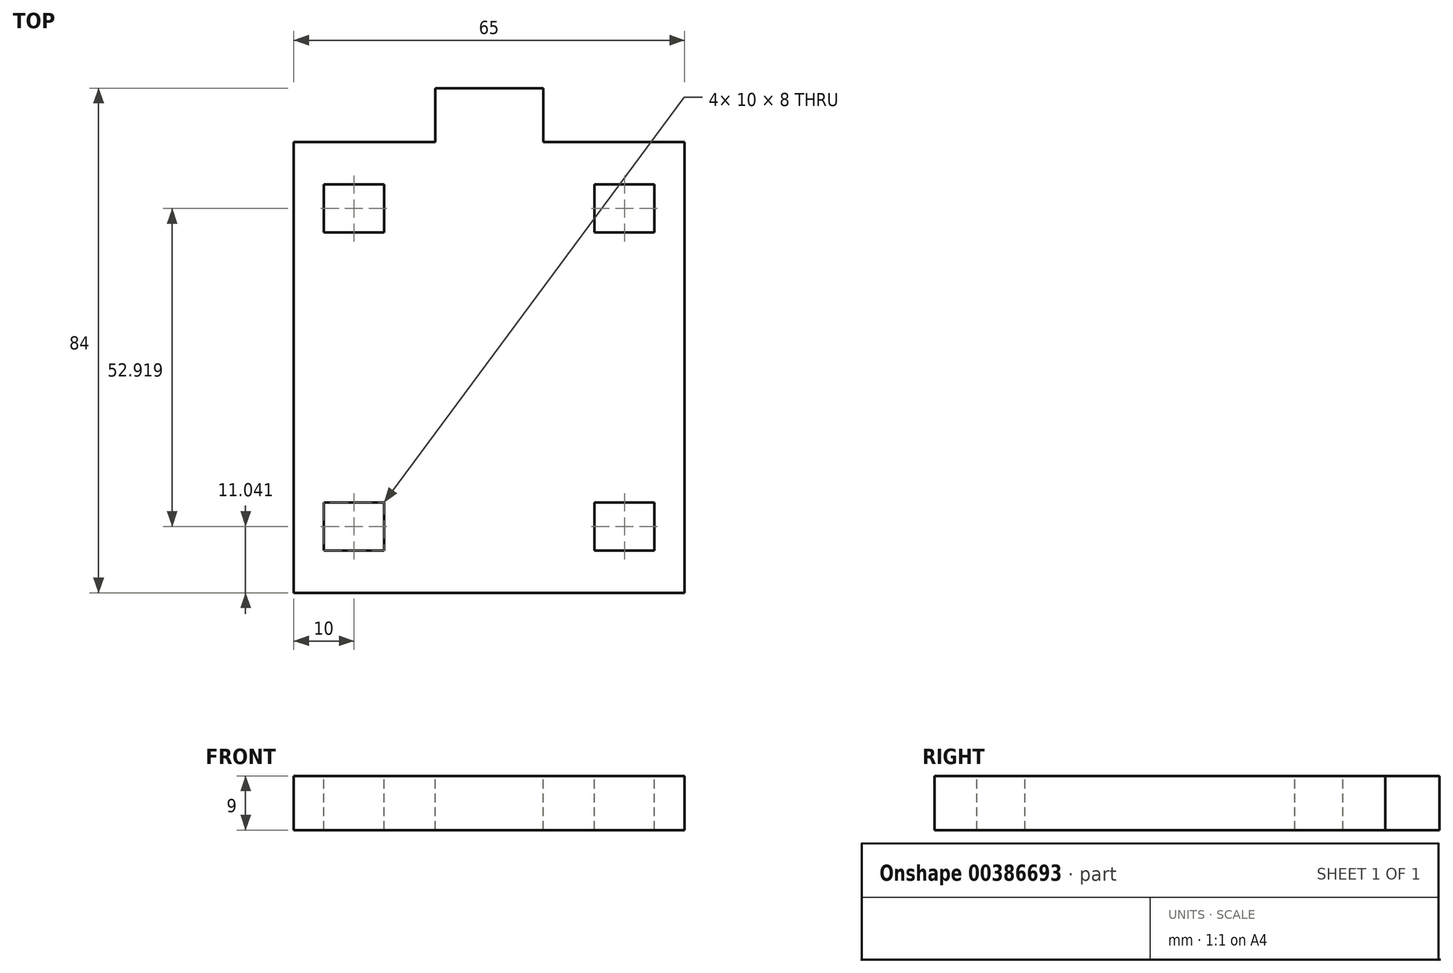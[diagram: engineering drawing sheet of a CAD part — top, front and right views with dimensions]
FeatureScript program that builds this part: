
annotation { "Feature Type Name" : "Feature", "Feature Type Description" : "" }
export const myFeature = defineFeature(function(context is Context, id is Id, definition is map)
    precondition{}
    {
        {
            var Q0;
            Q0=qCreatedBy(makeId("Top.planeOp"),FACE);
            var sketch = newSketch(context, id + "F0", { "sketchPlane" : qUnion([Q0])});
            skLineSegment(sketch, "E0.bottom", {"start": v(-32.5, 37.5) * mm, "end": v(32.5, 37.5) * mm});
            skLineSegment(sketch, "E0.top", {"start": v(-32.5, -37.5) * mm, "end": v(32.5, -37.5) * mm});
            skLineSegment(sketch, "E0.left", {"start": v(-32.5, 37.5) * mm, "end": v(-32.5, -37.5) * mm});
            skLineSegment(sketch, "E0.right", {"start": v(32.5, 37.5) * mm, "end": v(32.5, -37.5) * mm});
            skPoint(sketch, "E0.middle", {"position": v(0, 0) * mm});
            skSolve(sketch);
        }
        {
            var Q0;
            Q0 = qSketchRegion(id + "F0", true);
            extrude(context, id + "F1", {"entities" : qUnion([Q0]), "depth" : 9 * mm});
        }
        {
            var Q0;
            Q0=makeQuery(id+"F1.opExtrude","CAP_FACE",FACE,{"disambiguationData":[OSD([sQuery(id+"F0.wireOp",EDGE,"E0.bottom"),sQuery(id+"F0.wireOp",EDGE,"E0.top"),sQuery(id+"F0.wireOp",EDGE,"E0.left"),sQuery(id+"F0.wireOp",EDGE,"E0.right")])],"isStart":false});
            var sketch = newSketch(context, id + "F2", { "sketchPlane" : qUnion([Q0])});
            skLineSegment(sketch, "E1", {"start": v(0, 37.5) * mm, "end": v(0, 46.5) * mm, "construction": true});
            skLineSegment(sketch, "E2", {"start": v(0, 46.5) * mm, "end": v(9, 46.5) * mm});
            skLineSegment(sketch, "E3", {"start": v(9, 46.5) * mm, "end": v(9, 37.5) * mm});
            skLineSegment(sketch, "E4", {"start": v(9, 37.5) * mm, "end": v(0, 37.5) * mm});
            skLineSegment(sketch, "E5.MirrorCS", {"start": v(0, 46.5) * mm, "end": v(-9, 46.5) * mm});
            skLineSegment(sketch, "E6.MirrorCS", {"start": v(-9, 46.5) * mm, "end": v(-9, 37.5) * mm});
            skLineSegment(sketch, "E7.MirrorCS", {"start": v(-9, 37.5) * mm, "end": v(0, 37.5) * mm});
            skSolve(sketch);
        }
        {
            var Q0;
            Q0 = qSketchRegion(id + "F2", true);
            var Q1;
            Q1=makeQuery(id+"F1.opExtrude","CAP_FACE",FACE,{"disambiguationData":[OSD([sQuery(id+"F0.wireOp",EDGE,"E0.bottom"),sQuery(id+"F0.wireOp",EDGE,"E0.top"),sQuery(id+"F0.wireOp",EDGE,"E0.left"),sQuery(id+"F0.wireOp",EDGE,"E0.right")])],"isStart":true});
            extrude(context, id + "F3", {"entities" : qUnion([Q0]), "operationType" : NewBodyOperationType.ADD, "endBound" : BoundingType.UP_TO_SURFACE, "oppositeDirection" : true, "endBoundEntityFace" : qUnion([Q1]), "depth" : 25 * mm});
        }
        {
            var Q0;
            Q0=makeQuery(id+"F3.boolean.opBoolean","MERGE",FACE,{"derivedFrom":[makeQuery(id+"F1.opExtrude","CAP_FACE",FACE,{"disambiguationData":[OSD([sQuery(id+"F0.wireOp",EDGE,"E0.bottom"),sQuery(id+"F0.wireOp",EDGE,"E0.top"),sQuery(id+"F0.wireOp",EDGE,"E0.left"),sQuery(id+"F0.wireOp",EDGE,"E0.right")])],"isStart":false}),makeQuery(id+"F3.opExtrude","CAP_FACE",FACE,{"disambiguationData":[OSD([sQuery(id+"F2.wireOp",EDGE,"E2"),sQuery(id+"F2.wireOp",EDGE,"E3"),sQuery(id+"F2.wireOp",EDGE,"E4"),sQuery(id+"F2.wireOp",EDGE,"E5.MirrorCS"),sQuery(id+"F2.wireOp",EDGE,"E6.MirrorCS"),sQuery(id+"F2.wireOp",EDGE,"E7.MirrorCS")])],"isStart":true})]});
            var sketch = newSketch(context, id + "F4", { "sketchPlane" : qUnion([Q0])});
            skLineSegment(sketch, "E8", {"start": v(-32.5, 0) * mm, "end": v(-27.5, 0) * mm, "construction": true});
            skLineSegment(sketch, "E9", {"start": v(-27.5, 0) * mm, "end": v(-27.5, 30.46) * mm, "construction": true});
            skLineSegment(sketch, "E10.bottom", {"start": v(-27.5, 30.46) * mm, "end": v(-17.5, 30.46) * mm});
            skLineSegment(sketch, "E10.top", {"start": v(-27.5, 22.46) * mm, "end": v(-17.5, 22.46) * mm});
            skLineSegment(sketch, "E10.left", {"start": v(-27.5, 30.46) * mm, "end": v(-27.5, 22.46) * mm});
            skLineSegment(sketch, "E10.right", {"start": v(-17.5, 30.46) * mm, "end": v(-17.5, 22.46) * mm});
            skLineSegment(sketch, "E11", {"start": v(0, 37.32) * mm, "end": v(0, 0) * mm, "construction": true});
            skLineSegment(sketch, "E12", {"start": v(0, 0) * mm, "end": v(32.5, 0) * mm, "construction": true});
            skLineSegment(sketch, "E13.MirrorCS", {"start": v(27.5, 30.46) * mm, "end": v(17.5, 30.46) * mm});
            skLineSegment(sketch, "E14.MirrorCS", {"start": v(17.5, 30.46) * mm, "end": v(17.5, 22.46) * mm});
            skLineSegment(sketch, "E15.MirrorCS", {"start": v(27.5, 22.46) * mm, "end": v(17.5, 22.46) * mm});
            skLineSegment(sketch, "E16.MirrorCS", {"start": v(27.5, 0) * mm, "end": v(27.5, 30.46) * mm, "construction": true});
            skLineSegment(sketch, "E17.MirrorCS", {"start": v(27.5, -22.46) * mm, "end": v(17.5, -22.46) * mm});
            skLineSegment(sketch, "E18.MirrorCS", {"start": v(17.5, -30.46) * mm, "end": v(17.5, -22.46) * mm});
            skLineSegment(sketch, "E19.MirrorCS", {"start": v(27.5, -30.46) * mm, "end": v(17.5, -30.46) * mm});
            skLineSegment(sketch, "E20.MirrorCS", {"start": v(27.5, 0) * mm, "end": v(27.5, -30.46) * mm, "construction": true});
            skLineSegment(sketch, "E21.MirrorCS", {"start": v(-27.5, -22.46) * mm, "end": v(-17.5, -22.46) * mm});
            skLineSegment(sketch, "E22.MirrorCS", {"start": v(-17.5, -30.46) * mm, "end": v(-17.5, -22.46) * mm});
            skLineSegment(sketch, "E23.MirrorCS", {"start": v(-27.5, -30.46) * mm, "end": v(-17.5, -30.46) * mm});
            skLineSegment(sketch, "E24.MirrorCS", {"start": v(-27.5, 0) * mm, "end": v(-27.5, -30.46) * mm, "construction": true});
            skLineSegment(sketch, "E25", {"start": v(27.5, 30.46) * mm, "end": v(27.5, 22.46) * mm});
            skLineSegment(sketch, "E26", {"start": v(27.5, -22.46) * mm, "end": v(27.5, -30.46) * mm});
            skLineSegment(sketch, "E27", {"start": v(-27.5, -22.46) * mm, "end": v(-27.5, -30.46) * mm});
            skSolve(sketch);
        }
        {
            var Q0;
            Q0 = qSketchRegion(id + "F4", true);
            extrude(context, id + "F5", {"entities" : qUnion([Q0]), "operationType" : NewBodyOperationType.REMOVE, "endBound" : BoundingType.THROUGH_ALL, "oppositeDirection" : true, "depth" : 25 * mm});
        }
    });
